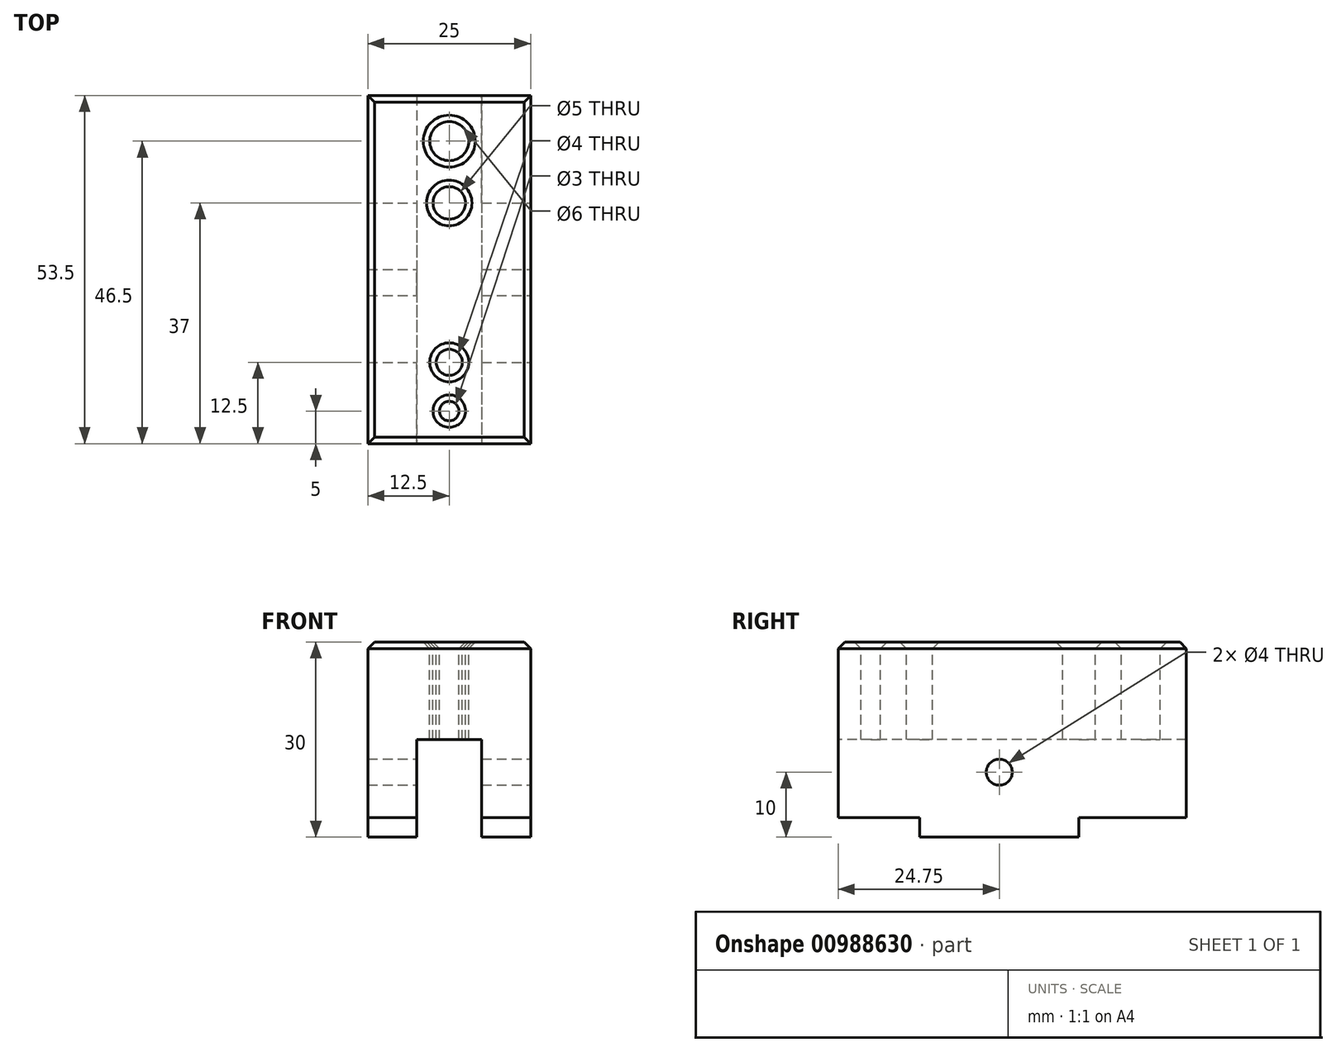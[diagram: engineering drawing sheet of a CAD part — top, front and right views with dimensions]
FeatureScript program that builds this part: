
annotation { "Feature Type Name" : "Feature", "Feature Type Description" : "" }
export const myFeature = defineFeature(function(context is Context, id is Id, definition is map)
    precondition{}
    {
        {
            var Q0;
            Q0=qCreatedBy(makeId("Top.planeOp"),FACE);
            var sketch = newSketch(context, id + "F0", { "sketchPlane" : qUnion([Q0])});
            skLineSegment(sketch, "E0.bottom", {"start": v(0, 0) * mm, "end": v(25, 0) * mm});
            skLineSegment(sketch, "E0.top", {"start": v(0, 53.5) * mm, "end": v(25, 53.5) * mm});
            skLineSegment(sketch, "E0.left", {"start": v(0, 0) * mm, "end": v(0, 53.5) * mm});
            skLineSegment(sketch, "E0.right", {"start": v(25, 0) * mm, "end": v(25, 53.5) * mm});
            skLineSegment(sketch, "E1", {"start": v(12.5, 53.5) * mm, "end": v(12.5, 0) * mm, "construction": true});
            skCircle(sketch, "E2", {"center": v(12.5, 5) * mm, "radius": 1.5 * mm});
            skCircle(sketch, "E3", {"center": v(12.5, 12.5) * mm, "radius": 2 * mm});
            skCircle(sketch, "E4", {"center": v(12.5, 37) * mm, "radius": 2.5 * mm});
            skCircle(sketch, "E5", {"center": v(12.5, 46.5) * mm, "radius": 3 * mm});
            skSolve(sketch);
        }
        {
            var Q0;
            Q0=makeQuery(id+"F0.imprint","IMPRINT",FACE,{"disambiguationData":[TD([[makeQuery(id+"F0.imprint","IMPRINT",EDGE,{"derivedFrom":sQuery(id+"F0.wireOp",EDGE,"E0.bottom")}),1.0]])]});
            extrude(context, id + "F1", {"entities" : qUnion([Q0]), "oppositeDirection" : true, "depth" : 30 * mm, "offsetDistance" : 25 * mm});
        }
        {
            var Q0;
            Q0=makeQuery(id+"F1.opExtrude","SWEPT_FACE",FACE,{"disambiguationData":[OSD([sQuery(id+"F0.wireOp",EDGE,"E0.bottom")])]});
            var sketch = newSketch(context, id + "F2", { "sketchPlane" : qUnion([Q0])});
            skLineSegment(sketch, "E6", {"start": v(0, -30) * mm, "end": v(7.5, -30) * mm});
            skLineSegment(sketch, "E7", {"start": v(7.5, -30) * mm, "end": v(7.5, -15) * mm});
            skLineSegment(sketch, "E8", {"start": v(7.5, -15) * mm, "end": v(17.5, -15) * mm});
            skLineSegment(sketch, "E9", {"start": v(17.5, -15) * mm, "end": v(17.5, -30) * mm});
            skLineSegment(sketch, "E10", {"start": v(17.5, -30) * mm, "end": v(25, -30) * mm});
            skLineSegment(sketch, "E11", {"start": v(25, -30) * mm, "end": v(7.5, -30) * mm});
            skSolve(sketch);
        }
        {
            var Q0;
            {var subQ0=sQuery(id+"F2.wireOp",EDGE,"E7");Q0=makeQuery(id+"F2.imprint","IMPRINT",FACE,{"disambiguationData":[TD([[makeQuery(id+"F2.imprint","IMPRINT",EDGE,{"derivedFrom":subQ0}),-1.0]])]});}
            extrude(context, id + "F3", {"entities" : qUnion([Q0]), "operationType" : NewBodyOperationType.REMOVE, "endBound" : BoundingType.THROUGH_ALL, "oppositeDirection" : true, "depth" : 25 * mm, "offsetDistance" : 25 * mm});
        }
        {
            var Q0;
            Q0=makeQuery(id+"F1.opExtrude","SWEPT_FACE",FACE,{"disambiguationData":[OSD([sQuery(id+"F0.wireOp",EDGE,"E0.right")])]});
            var sketch = newSketch(context, id + "F4", { "sketchPlane" : qUnion([Q0])});
            skLineSegment(sketch, "E12.bottom", {"start": v(53.5, -30) * mm, "end": v(37, -30) * mm});
            skLineSegment(sketch, "E12.top", {"start": v(53.5, -27) * mm, "end": v(37, -27) * mm});
            skLineSegment(sketch, "E12.left", {"start": v(53.5, -30) * mm, "end": v(53.5, -27) * mm});
            skLineSegment(sketch, "E12.right", {"start": v(37, -30) * mm, "end": v(37, -27) * mm});
            skLineSegment(sketch, "E13.bottom", {"start": v(53.5, -27) * mm, "end": v(46.5, -27) * mm});
            skLineSegment(sketch, "E13.top", {"start": v(53.5, -24) * mm, "end": v(46.5, -24) * mm});
            skLineSegment(sketch, "E13.left", {"start": v(53.5, -27) * mm, "end": v(53.5, -24) * mm});
            skLineSegment(sketch, "E13.right", {"start": v(46.5, -27) * mm, "end": v(46.5, -24) * mm});
            skLineSegment(sketch, "E14.bottom", {"start": v(0, -30) * mm, "end": v(12.5, -30) * mm});
            skLineSegment(sketch, "E14.top", {"start": v(0, -27) * mm, "end": v(12.5, -27) * mm});
            skLineSegment(sketch, "E14.left", {"start": v(0, -30) * mm, "end": v(0, -27) * mm});
            skLineSegment(sketch, "E14.right", {"start": v(12.5, -30) * mm, "end": v(12.5, -27) * mm});
            skLineSegment(sketch, "E15.bottom", {"start": v(0, -27) * mm, "end": v(5, -27) * mm});
            skLineSegment(sketch, "E15.top", {"start": v(0, -24) * mm, "end": v(5, -24) * mm});
            skLineSegment(sketch, "E15.left", {"start": v(0, -27) * mm, "end": v(0, -24) * mm});
            skLineSegment(sketch, "E15.right", {"start": v(5, -27) * mm, "end": v(5, -24) * mm});
            skSolve(sketch);
        }
        {
            var Q0;
            Q0=makeQuery(id+"F4.imprint","IMPRINT",FACE,{"disambiguationData":[TD([[makeQuery(id+"F4.imprint","IMPRINT",EDGE,{"derivedFrom":sQuery(id+"F4.wireOp",EDGE,"E13.bottom")}),-1.0]])]});
            var Q1;
            Q1=makeQuery(id+"F4.imprint","IMPRINT",FACE,{"disambiguationData":[TD([[makeQuery(id+"F4.imprint","IMPRINT",EDGE,{"derivedFrom":sQuery(id+"F4.wireOp",EDGE,"E12.bottom")}),1.0]])]});
            var Q2;
            Q2=makeQuery(id+"F4.imprint","IMPRINT",FACE,{"disambiguationData":[TD([[makeQuery(id+"F4.imprint","IMPRINT",EDGE,{"derivedFrom":sQuery(id+"F4.wireOp",EDGE,"E14.bottom")}),1.0]])]});
            var Q3;
            Q3=makeQuery(id+"F4.imprint","IMPRINT",FACE,{"disambiguationData":[TD([[makeQuery(id+"F4.imprint","IMPRINT",EDGE,{"derivedFrom":sQuery(id+"F4.wireOp",EDGE,"E15.bottom")}),1.0]])]});
            extrude(context, id + "F5", {"entities" : qUnion([Q0, Q1, Q2, Q3]), "operationType" : NewBodyOperationType.REMOVE, "endBound" : BoundingType.THROUGH_ALL, "oppositeDirection" : true, "depth" : 25 * mm, "offsetDistance" : 25 * mm});
        }
        {
            var Q0;
            Q0=makeQuery(id+"F1.opExtrude","CAP_EDGE",EDGE,{"disambiguationData":[OSD([sQuery(id+"F0.wireOp",EDGE,"E2")])],"isStart":true});
            var Q1;
            Q1=makeQuery(id+"F1.opExtrude","CAP_EDGE",EDGE,{"disambiguationData":[OSD([sQuery(id+"F0.wireOp",EDGE,"E3")])],"isStart":true});
            var Q2;
            Q2=makeQuery(id+"F1.opExtrude","CAP_EDGE",EDGE,{"disambiguationData":[OSD([sQuery(id+"F0.wireOp",EDGE,"E4")])],"isStart":true});
            var Q3;
            Q3=makeQuery(id+"F1.opExtrude","CAP_EDGE",EDGE,{"disambiguationData":[OSD([sQuery(id+"F0.wireOp",EDGE,"E5")])],"isStart":true});
            var Q4;
            Q4=makeQuery(id+"F1.opExtrude","CAP_EDGE",EDGE,{"disambiguationData":[OSD([sQuery(id+"F0.wireOp",EDGE,"E0.bottom")])],"isStart":true});
            var Q5;
            Q5=makeQuery(id+"F1.opExtrude","CAP_FACE",FACE,{"disambiguationData":[OSD([sQuery(id+"F0.wireOp",EDGE,"E0.bottom"),sQuery(id+"F0.wireOp",EDGE,"E0.top"),sQuery(id+"F0.wireOp",EDGE,"E0.left"),sQuery(id+"F0.wireOp",EDGE,"E0.right"),sQuery(id+"F0.wireOp",EDGE,"E2"),sQuery(id+"F0.wireOp",EDGE,"E3"),sQuery(id+"F0.wireOp",EDGE,"E4"),sQuery(id+"F0.wireOp",EDGE,"E5")])],"isStart":true});
            chamfer(context, id + "F6", {"entities" : qUnion([Q0, Q1, Q2, Q3, Q4, Q5]), "width" : 1 * mm, "tangentPropagation" : true});
        }
        {
            var Q0;
            Q0=makeQuery(id+"F1.opExtrude","SWEPT_FACE",FACE,{"disambiguationData":[OSD([sQuery(id+"F0.wireOp",EDGE,"E0.right")])]});
            var sketch = newSketch(context, id + "F7", { "sketchPlane" : qUnion([Q0])});
            skLineSegment(sketch, "E16.0", {"start": v(53.5, -15) * mm, "end": v(0, -15) * mm, "construction": true});
            skLineSegment(sketch, "E17", {"start": v(24.75, -30) * mm, "end": v(24.75, -15) * mm, "construction": true});
            skCircle(sketch, "E18", {"center": v(24.75, -20) * mm, "radius": 2 * mm});
            skPoint(sketch, "E19", {"position": v(24.75, -22.5) * mm});
            skSolve(sketch);
        }
        {
            var Q0;
            Q0=makeQuery(id+"F7.imprint","IMPRINT",FACE,{"disambiguationData":[TD([[makeQuery(id+"F7.imprint","IMPRINT",EDGE,{"derivedFrom":sQuery(id+"F7.wireOp",EDGE,"E18")}),1.0]])]});
            extrude(context, id + "F8", {"entities" : qUnion([Q0]), "operationType" : NewBodyOperationType.REMOVE, "endBound" : BoundingType.THROUGH_ALL, "oppositeDirection" : true, "depth" : 25 * mm, "offsetDistance" : 25 * mm});
        }
    });
